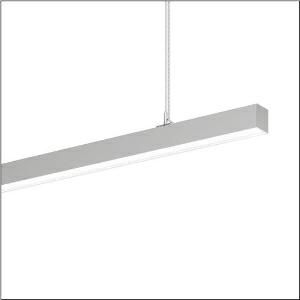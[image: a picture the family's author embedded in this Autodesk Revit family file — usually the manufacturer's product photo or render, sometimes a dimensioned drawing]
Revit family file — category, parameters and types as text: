
# Revit family: silica_r__21_51mx30db45sb_ca73
name_source: partatom
category: Lighting Fixtures
units: mm (PartAtom-declared; Revit-internal decimal feet)

## family parameters
Cut with Voids When Loaded = No
Host = Face
Light Source = No
Part Type = Normal
Room Calculation Point = No
Round Connector Dimension = Use Diameter
Shared = No

## types (1)
- --- (1 x LED, 5260 lm, 32 W, 4000K)
    Apparent Load = 32 VA
    CIE Flux Codes = 47 79 96 57 100
    Color Rendering = 80
    Color Temperature = 4000K
    Default Elevation = 1800 mm
    Description = Silica® 21, office luminaire, primary optical cover: cover, of PMMA, opal, light emission: direct/indirect distribution, primary light characteristic: symmetric, installation type: suspended mounting, LED, rated luminous flux: 5.260lm, luminous efficacy: 164lm/W, light colour: 840, colour temperature: 4000K, with terminal, 3+2-pole, max. 2.5mm², mains connection: 220..240V, AC, 50/60Hz, rated input power: 32W, luminaire housing, of aluminium, metallic grey (RAL 9006), length: 1.504mm, width: 53mm, height: 53mm, protection rating (complete): IP20, insulation class (complete): insulation class I (protective earthing), certification: CE, permissible operating ambient temperature: 0..+35°C, standard: EN 50419, packaging unit: 1 piece
    Height = 53 mm
    Lamp = 1 x LED
    Lamp Light Flux = 5260 lm
    Lamp Power = 32 W
    Lamp count = 1
    Length = 1504 mm
    Luminous efficacy = 164 lm/W
    Manufacturer = Siteco
    ModVariant = No
    Model = 51MX30DB45SB
    Mounting Place = Ceiling
    Mounting Type = Pendant
    Number of Poles = 1
    OnlyDefault = Yes
    Power Factor = 1
    Product Name = Silica® 21
    Product group = office luminaire | ceiling pendant
    ProductGroupID = 902
    Protection Class = Protection class I
    Protection Degree = IP 20
    RLX_Detail_Level = 1
    RLX_Emergency_Light_Flux = 0 lm
    RLX_Emergency_Type = 0
    RLX_Emergency_Type_DB = No
    RlxData = <blob elided: 23341 chars, md5=b2b017f8>
    Socket = socket
    Standby Power = 0 W
    System Light Flux = 5260 lm
    System Power = 32 W
    Type Comments = factory setting: luminous flux: 100 % | dim-lin: 254 | 218 mA
    Type Image = l_1313621.jpg
    URL = http://relux.com
    VarID = @adj_065133
    Voltage = 0 V
    Weight = 0.00 kg
    Width = 53 mm

## geometry (parser evidence)
native form markers: Blend x4, Sweep x11
no freeform markers — native parametric forms only
